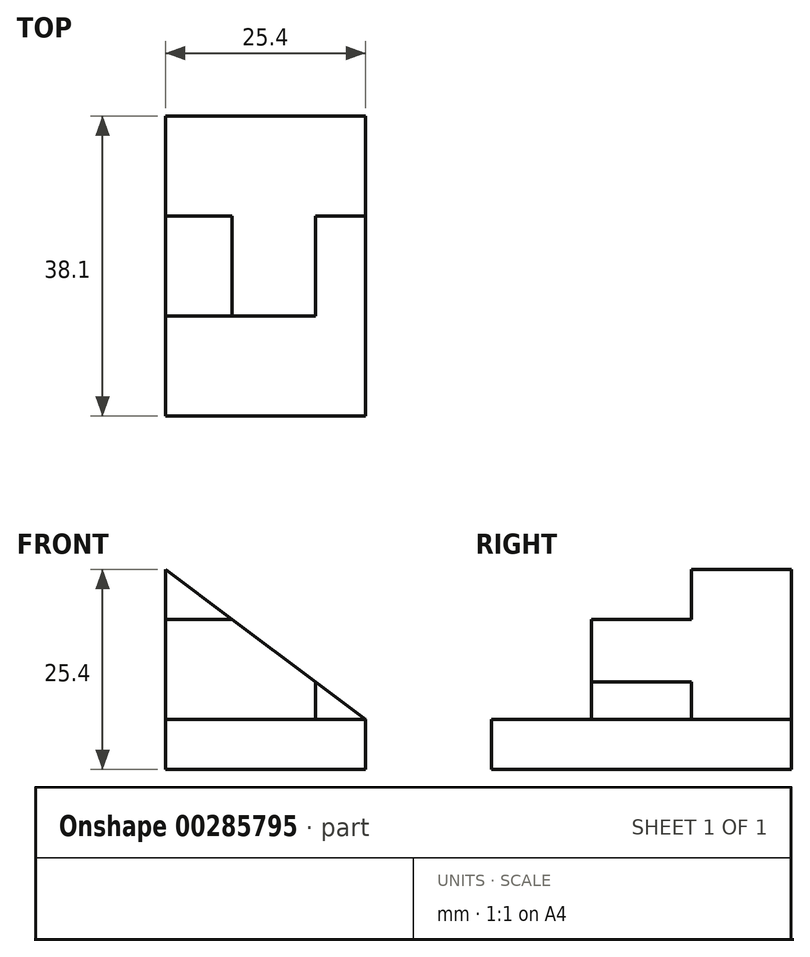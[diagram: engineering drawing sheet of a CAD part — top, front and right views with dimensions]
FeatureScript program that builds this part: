
annotation { "Feature Type Name" : "Feature", "Feature Type Description" : "" }
export const myFeature = defineFeature(function(context is Context, id is Id, definition is map)
    precondition{}
    {
        {
            var Q0;
            Q0=qCreatedBy(makeId("Front.planeOp"),FACE);
            var sketch = newSketch(context, id + "F0", { "sketchPlane" : qUnion([Q0])});
            skLineSegment(sketch, "E0", {"start": v(0, 0) * mm, "end": v(0, 25.4) * mm});
            skLineSegment(sketch, "E1", {"start": v(25.4, 0) * mm, "end": v(0, 0) * mm});
            skLineSegment(sketch, "E2", {"start": v(0, 25.4) * mm, "end": v(25.4, 6.35) * mm});
            skLineSegment(sketch, "E3", {"start": v(25.4, 6.35) * mm, "end": v(25.4, 0) * mm});
            skLineSegment(sketch, "E4", {"start": v(0, 6.35) * mm, "end": v(25.4, 6.35) * mm});
            skLineSegment(sketch, "E5", {"start": v(0, 19.05) * mm, "end": v(8.47, 19.05) * mm});
            skLineSegment(sketch, "E6", {"start": v(19.05, 11.11) * mm, "end": v(19.05, 6.35) * mm});
            skSolve(sketch);
        }
        {
            var Q0;
            {var subQ5=sQuery(id+"F0.wireOp",EDGE,"E1");Q0=makeQuery(id+"F0.imprint","IMPRINT",FACE,{"disambiguationData":[TD([[makeQuery(id+"F0.imprint","IMPRINT",EDGE,{"derivedFrom":subQ5}),-1.0]])]});}
            extrude(context, id + "F1", {"entities" : qUnion([Q0]), "depth" : 38.1 * mm});
        }
        {
            var Q0;
            {var subQ4=sQuery(id+"F0.wireOp",EDGE,"E5");Q0=makeQuery(id+"F0.imprint","IMPRINT",FACE,{"disambiguationData":[TD([[makeQuery(id+"F0.imprint","IMPRINT",EDGE,{"derivedFrom":subQ4}),-1.0]])]});}
            extrude(context, id + "F2", {"entities" : qUnion([Q0]), "operationType" : NewBodyOperationType.ADD, "depth" : 25.4 * mm});
        }
        {
            var Q0;
            {var subQ3=sQuery(id+"F0.wireOp",EDGE,"E5");Q0=makeQuery(id+"F0.imprint","IMPRINT",FACE,{"disambiguationData":[TD([[makeQuery(id+"F0.imprint","IMPRINT",EDGE,{"derivedFrom":subQ3}),1.0]])]});}
            extrude(context, id + "F3", {"entities" : qUnion([Q0]), "operationType" : NewBodyOperationType.ADD, "depth" : 12.7 * mm});
        }
        {
            var Q0;
            {var subQ3=sQuery(id+"F0.wireOp",EDGE,"E6");Q0=makeQuery(id+"F0.imprint","IMPRINT",FACE,{"disambiguationData":[TD([[makeQuery(id+"F0.imprint","IMPRINT",EDGE,{"derivedFrom":subQ3}),1.0]])]});}
            extrude(context, id + "F4", {"entities" : qUnion([Q0]), "operationType" : NewBodyOperationType.ADD, "depth" : 12.7 * mm});
        }
    });
